# Revit family: 3-60-xx Cirro Pendant
name_source: partatom
category: Generic Models
revit_build: Autodesk Revit 2018 (Build: 20170223_1515(x64)
units: mm (PartAtom-declared; Revit-internal decimal feet)

## family parameters
Always vertical = No
Can host rebar = No
Cut with Voids When Loaded = No
Part Type = Undefined
Room Calculation Point = No
Round Connector Dimension = Use Diameter
Shared = Yes

## types (2) — shared parameters
Color = 3000 K
Lamp = LED Array
Main Diffuser = Oxygen Lighting - Diffuser - Matte White Acrylic
Manufacturer = Oxygen - Lighting & Fans
Model = 3-60-6 Cirro Pendant
Pendant Heigth = 8.66 "
References = Ref. 3 = 120 V / Ref. 37 = 277 V
URL = www.oxygenlighting.com
Voltage Input = 120 V or 277 V - 50/60 Hz
Wattage Comments = 445.0 W at 120 V

## per-type parameters (varying)
| type | Metal Finish | Wattage | Wires Heigth |
| 3-60-15 / Black - Matte White Acrylic | Oxygen Lighting - Metal Finish - 15 - Black | 95 W | 19.21 " |
| 3-60-6 / White - Matte White Acrylic | Oxygen Lighting - Metal Finish - 06 - White | 44 W | 18.46 " |

## geometry (parser evidence)
native form markers: Extrusion x1, Sweep x7
no freeform markers — native parametric forms only
